# Revit family: GA-66_SET1
name_source: partatom
category: Plumbing Fixtures
revit_build: Autodesk Revit Architecture 2012 (Build: 20110309_2315(x64)
units: mm (PartAtom-declared; Revit-internal decimal feet)

## types (1)
- GA-661SET1
    Assembly Code = D2010
    CW Connection = Yes
    CWFU = 0
    Cost = 0 $
    Default Elevation = 0' - 0"
    Description = 1 x undertile diverter mixer + shower arm + head and bath spout.
    Diverter = S-950-7CP
    Gala classic handle = S-650/3
    HW Connection = Yes
    HWFU = 0
    Keynote = Undertile bath/shower diverter mixer
    Manufacturer = COBRA
    Material = Chrome - Polished
    Model = GA-661SET1
    Raised cartridge = S-SE950-1-R
    Range = Gala
    Shower arm = P-024
    Shower head = P-0681
    Type Comments = SANS 1480
    URL = http://www.cobra.co.za
    Undertile bath/shower diverter mixer = GA-661
    Vent Connection = No
    WFU = 0
    Waste Connection = No

## geometry (parser evidence)
native form markers: Blend x2
no freeform markers — native parametric forms only
